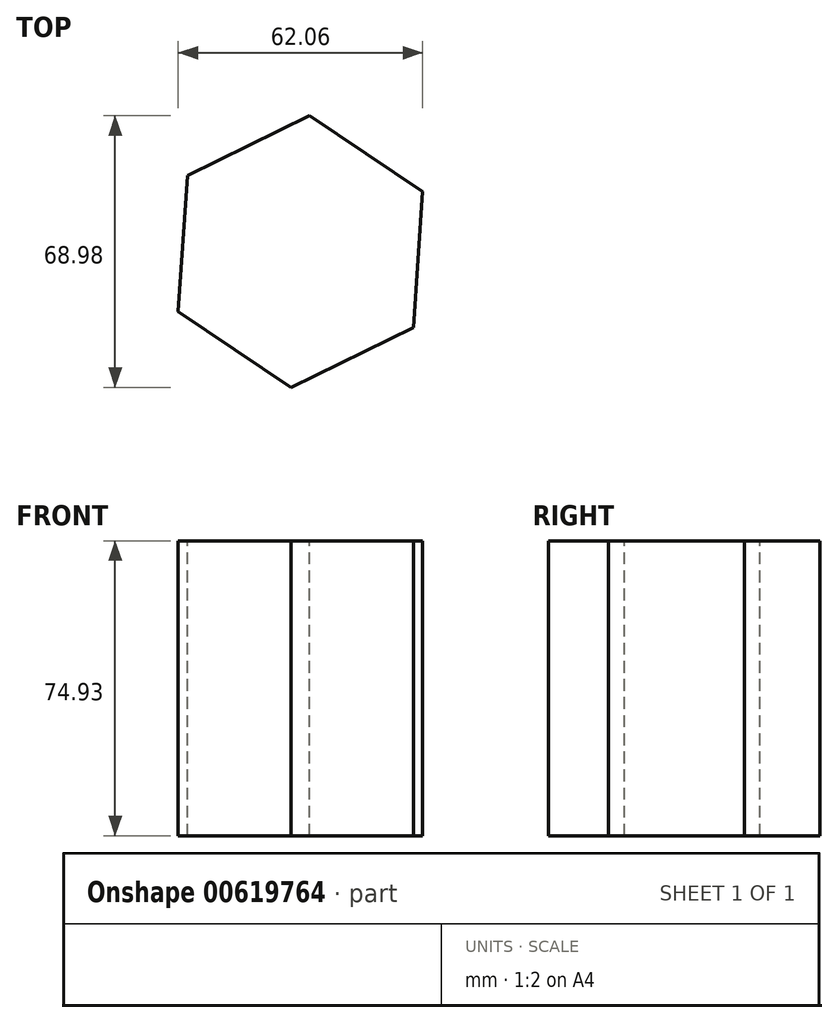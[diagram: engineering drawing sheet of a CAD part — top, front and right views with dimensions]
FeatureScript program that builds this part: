
annotation { "Feature Type Name" : "Feature", "Feature Type Description" : "" }
export const myFeature = defineFeature(function(context is Context, id is Id, definition is map)
    precondition{}
    {
        {
            var Q0;
            Q0=qCreatedBy(makeId("Top.planeOp"),FACE);
            var sketch = newSketch(context, id + "F0", { "sketchPlane" : qUnion([Q0])});
            skCircle(sketch, "E0.cCircle", {"center": v(0, 0) * mm, "radius": 29.94 * mm, "construction": true});
            skLineSegment(sketch, "E0.0", {"start": v(-28.71, 19.25) * mm, "end": v(2.32, 34.5) * mm});
            skLineSegment(sketch, "E0.1", {"start": v(2.32, 34.5) * mm, "end": v(31.03, 15.24) * mm});
            skLineSegment(sketch, "E0.2", {"start": v(31.03, 15.24) * mm, "end": v(28.71, -19.25) * mm});
            skLineSegment(sketch, "E0.3", {"start": v(28.71, -19.25) * mm, "end": v(-2.32, -34.5) * mm});
            skLineSegment(sketch, "E0.4", {"start": v(-2.32, -34.5) * mm, "end": v(-31.03, -15.24) * mm});
            skLineSegment(sketch, "E0.5", {"start": v(-31.03, -15.24) * mm, "end": v(-28.71, 19.25) * mm});
            skPoint(sketch, "E0.0.midPoint", {"position": v(-13.2, 26.87) * mm});
            skSolve(sketch);
        }
        {
            var Q0;
            Q0=makeQuery(id+"F0.imprint","IMPRINT",FACE,{"disambiguationData":[TD([[makeQuery(id+"F0.imprint","IMPRINT",EDGE,{"derivedFrom":sQuery(id+"F0.wireOp",EDGE,"E0.0")}),-1.0]])]});
            extrude(context, id + "F1", {"entities" : qUnion([Q0]), "oppositeDirection" : true, "depth" : 74.93 * mm, "offsetDistance" : 25.4 * mm});
        }
    });
